# Revit family: 1GAHP-WS Indoor
name_source: partatom
category: Wyposażenie mechaniczne
revit_build: Autodesk Revit 2015 (Build: 20160512_1515(x64)
units: mm (PartAtom-declared; Revit-internal decimal feet)

## types (1)
- GAHP-WS
    Autor = www.archispace.pl
    Ciśnienie akustyczne w odległości 5 metrów = 44,1 dB (A)
    Ciśnienie gazu zasilającego (LPG G30/G31) = 32 - 42 mbar
    Ciśnienie gazu zasilającego (gaz ziemny G20) = 17 - 23 mbar
    Dokumentacja techniczna = http://www.gazuno.pl
    Głębokość = 690 mm  [stored 2.26378 ft]
    IP = X5D
    Klasyfikacja obciążenia = Inne
    Maksymalne ciśnienie robocze = 4 pasek
    Materiał obudowa = Robur_CashmereGrey
    Materiał podstawa = Robur_Stal
    Max. ciśnienie w układzie absorpcyjnym = 35 bar
    Max. przepływ kondensatu = 4 l/h
    Max. przepływ medium w odnawialnym źródle = 1.306 L/s
    Max. przepływ wody grzewczej = 1.111 L/s
    Max. temperatura medium na wyjściu z odnawialnego źródła = 45 °C
    Max. temperatura powietrza zewnętrznego (tryb grzania) = 45 °C
    Max. temperatura wody na wejściu do urządzenia = 55 °C
    Max. temperatura wody na wyjściu z urządzenia = 65 °C
    Min. przepływ medium w odnawialnym źródle = 0.639 L/s
    Min. przepływ wody grzewczej = 0.389 L/s
    Min. temperatura medium na wejściu do odnawialnego źródła = 3 °C
    Min. temperatura powietrza zewnętrznego (tryb grzania) = 0 °C
    Min. temperatura wody na wejściu do urządzenia (podczas pracy ciągłej) = 20 °C
    Moc elektryczna = 410 W
    Model = GAHP-WS
    Napięcie zasilania = 230 V
    Nominalna moc grzewcza palnika = 25700 W
    Nominalny przepływ medium w odnawialnym źródle = 0.792 L/s
    Nominalny przepływ wody grzewczej = 0.992 L/s
    Nominalny spadek ciśnienia wody grzewczej = 0.57 pasek
    Obciążenie pozorne = 410 VA
    Opis = Gazowa, absorpcyjna pompa ciepła woda/woda. Zasilana gazem i energią odnawialną.
    Producent = Robur
    Rzeczywista moc grzewcza palnika = 25200 W
    Spadek ciśnienia medium przy nominalnym przepływie = 0.38 pasek
    Sposób instalacji = C13, C33, C43, C53, C63, C83, B23P, B33
    Szerokość = 848 mm  [stored 2.78215 ft]
    URL = www.gazuno.pl
    Waga = 300.00 kg
    Waga płynu roboczego - amoniak R717 = 7.70 kg
    Waga płynu roboczego - woda = 10.00 kg
    Współczynnik mocy = 1
    Wysokość = 1278 mm  [stored 4.19291 ft]

note: [stored X ft] marks values corroborated as IEEE doubles in the binary element streams (Revit-internal decimal feet)
